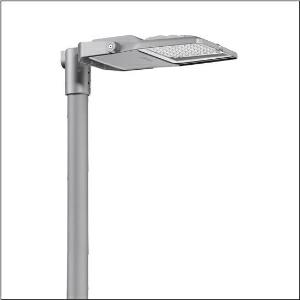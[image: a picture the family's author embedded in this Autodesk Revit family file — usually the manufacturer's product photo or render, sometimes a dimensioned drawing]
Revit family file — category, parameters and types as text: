
# Revit family: floodlight_fl_21_iq_mini___pl43_5xa7771b2a3a_6d21
name_source: partatom
category: Lighting Fixtures
units: mm (PartAtom-declared; Revit-internal decimal feet)

## family parameters
Cut with Voids When Loaded = No
Host = Face
Light Source = No
Part Type = Normal
Room Calculation Point = No
Round Connector Dimension = Use Diameter
Shared = No

## types (1)
- --- (1 x LED, 6400 lm, 45.5 W, 3000K)
    Apparent Load = 46 VA
    CIE Flux Codes = 27 78 99 100 100
    Color Rendering = 70
    Color Temperature = 3000K
    Default Elevation = 1800 mm
    Description = Floodlight FL 21 iQ mini, floodlight, primary light control with lens, of PMMA, primary optical cover: protective disc, of toughened safety glass, transparent, light distribution: PL43, light emission: direct distribution, installation type: surface-mounted, lamps: LED, High Power LED, rated values: 6.400lm | 45,5W | 140,7lm/W (begin service life); end service life: 6.400lm | 48W; at 50% lumin. flux: 3.200lm | 21,5W | 148,8lm/W, colour temperature: 3000K, colour rendering: CRI > 70, light colour: 730, light setting 1 begin service life: 100% | 6.400lm | 45,5W | 140,7lm/W | 3.000K, light setting 1 end service life: 48W, further light settings possible, control: Auto-Match, Temp-Guard, Lumen-Switch, Night-Set, Smart-Wire, Light-Fading, Desk-Remote (wireless, voltage-free reading and setting of iQ features in the workshop via application-optimized NFC function/RFID function), optimised constant luminous flux control (CLO 2.0), with terminal, 6-pole, mains connection: 220..240V, AC, 50/60Hz, luminaire housing, of diecast aluminium, powder-coated, Siteco® metallic grey (DB 702S), corrosivity category C5 mid according to DIN EN ISO 12944suitable for swimming poolschlorine-resistant, sealing non-destructively replaceable, please order mast flange separately, mast bracket, of steel, galvanised, powder-coated, Siteco® metallic grey (DB 702S), protection rating (complete): IP66, insulation class (complete): insulation class II (safety insulation), certification: CE, ENEC, VDE, protection symbol: D, impact resistance: IK08, permissible operating ambient temperature: -40..+40°C, permissible operating ambient temperature for outdoor applications: -40..+50°C, standard: DIN EN 12944, LABS conformity tested according to VDMA 24364:2018-05, packaging unit: 1 piece

Light Distribution: PL43
    Height = 70 mm
    Lamp = 1 x LED
    Lamp Light Flux = 6400 lm
    Lamp Power = 45.5 W
    Lamp count = 1
    Length = 485 mm
    Luminous efficacy = 141 lm/W
    Manufacturer = Siteco
    ModVariant = No
    Model = 5XA7771B2A3A
    Number of Poles = 1
    OnlyDefault = Yes
    Power Factor = 1
    Product Name = Floodlight FL 21 iQ mini | PL43
    Product group = floodlight | pylon annexe
    ProductGroupID = 6201
    Protection Class = Protection class II
    Protection Degree = IP 66
    RLX_Detail_Level = 1
    RLX_Emergency_Light_Flux = 0 lm
    RLX_Emergency_Type = 0
    RLX_Emergency_Type_DB = No
    RlxData = <blob elided: 101249 chars, md5=f5726030>
    Socket = socket
    Standby Power = 0 W
    System Light Flux = 6400 lm
    System Power = 46 W
    Type Comments = factory setting: luminous flux: 100 % | dim-lin: 254 | 463 mA
    Type Image = l_1007125.jpg
    URL = http://relux.com
    VarID = @adj_166249
    Voltage = 0 V
    Weight = 0.00 kg
    Width = 337 mm

## geometry (parser evidence)
native form markers: Blend x4, Sweep x12
no freeform markers — native parametric forms only
